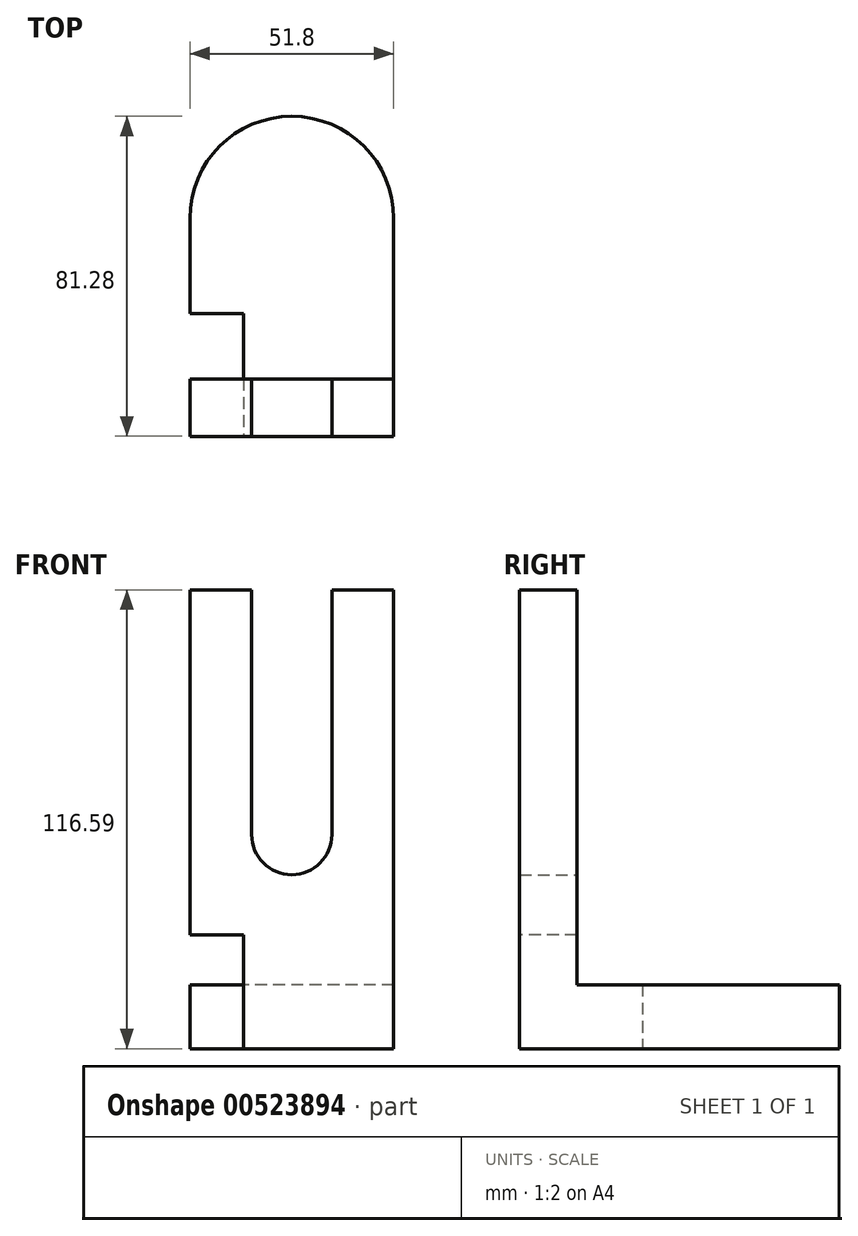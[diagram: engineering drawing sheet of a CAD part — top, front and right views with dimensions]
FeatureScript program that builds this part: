
annotation { "Feature Type Name" : "Feature", "Feature Type Description" : "" }
export const myFeature = defineFeature(function(context is Context, id is Id, definition is map)
    precondition{}
    {
        {
            var Q0;
            Q0=qCreatedBy(makeId("Top.planeOp"),FACE);
            var sketch = newSketch(context, id + "F0", { "sketchPlane" : qUnion([Q0])});
            skLineSegment(sketch, "E0.bottom", {"start": v(25.9, -27.7) * mm, "end": v(-25.9, -27.7) * mm});
            skLineSegment(sketch, "E0.left", {"start": v(25.9, -27.7) * mm, "end": v(25.9, 27.7) * mm});
            skLineSegment(sketch, "E0.right", {"start": v(-25.9, -27.7) * mm, "end": v(-25.9, 27.7) * mm});
            skPoint(sketch, "E0.middle", {"position": v(0, 0) * mm});
            skArc(sketch, "E1", {"start": v(-25.9, 27.7) * mm, "mid": v(0, 53.6) * mm, "end": v(25.9, 27.7) * mm});
            skSolve(sketch);
        }
        {
            var Q0;
            Q0=makeQuery(id+"F0.imprint","IMPRINT",FACE,{"disambiguationData":[TD([[makeQuery(id+"F0.imprint","IMPRINT",EDGE,{"derivedFrom":sQuery(id+"F0.wireOp",EDGE,"E0.bottom")}),-1.0]])]});
            extrude(context, id + "F1", {"entities" : qUnion([Q0]), "depth" : 16.26 * mm, "offsetDistance" : 25.4 * mm});
        }
        {
            var Q0;
            Q0=makeQuery(id+"F1.opExtrude","CAP_FACE",FACE,{"disambiguationData":[OSD([sQuery(id+"F0.wireOp",EDGE,"E0.bottom"),sQuery(id+"F0.wireOp",EDGE,"E0.left"),sQuery(id+"F0.wireOp",EDGE,"E0.right"),sQuery(id+"F0.wireOp",EDGE,"E1")])],"isStart":false});
            var sketch = newSketch(context, id + "F2", { "sketchPlane" : qUnion([Q0])});
            skLineSegment(sketch, "E2.bottom", {"start": v(25.9, -27.7) * mm, "end": v(-25.9, -27.7) * mm});
            skLineSegment(sketch, "E2.top", {"start": v(25.9, -13.13) * mm, "end": v(-25.9, -13.13) * mm});
            skLineSegment(sketch, "E2.left", {"start": v(25.9, -27.7) * mm, "end": v(25.9, -13.13) * mm});
            skLineSegment(sketch, "E2.right", {"start": v(-25.9, -27.7) * mm, "end": v(-25.9, -13.13) * mm});
            skSolve(sketch);
        }
        {
            var Q0;
            Q0=makeQuery(id+"F2.imprint","IMPRINT",FACE,{"disambiguationData":[TD([[makeQuery(id+"F2.imprint","IMPRINT",EDGE,{"derivedFrom":sQuery(id+"F2.wireOp",EDGE,"E2.bottom")}),-1.0]])]});
            extrude(context, id + "F3", {"entities" : qUnion([Q0]), "operationType" : NewBodyOperationType.ADD, "depth" : 100.33 * mm, "offsetDistance" : 25.4 * mm});
        }
        {
            var Q0;
            Q0=makeQuery(id+"F3.opExtrude","SWEPT_FACE",FACE,{"disambiguationData":[OSD([sQuery(id+"F2.wireOp",EDGE,"E2.top")])]});
            var sketch = newSketch(context, id + "F4", { "sketchPlane" : qUnion([Q0])});
            skLineSegment(sketch, "E3.top", {"start": v(10.2, 116.52) * mm, "end": v(-10.2, 116.52) * mm});
            skLineSegment(sketch, "E3.left", {"start": v(10.2, 54.38) * mm, "end": v(10.2, 116.52) * mm});
            skLineSegment(sketch, "E3.right", {"start": v(-10.2, 54.38) * mm, "end": v(-10.2, 116.52) * mm});
            skPoint(sketch, "E3.middle", {"position": v(0, 85.45) * mm});
            skArc(sketch, "E4", {"start": v(10.2, 54.38) * mm, "mid": v(0, 44.18) * mm, "end": v(-10.2, 54.38) * mm});
            skSolve(sketch);
        }
        {
            var Q0;
            Q0=makeQuery(id+"F4.imprint","IMPRINT",FACE,{"disambiguationData":[TD([[makeQuery(id+"F4.imprint","IMPRINT",EDGE,{"derivedFrom":sQuery(id+"F4.wireOp",EDGE,"E3.top")}),1.0]])]});
            extrude(context, id + "F5", {"entities" : qUnion([Q0]), "operationType" : NewBodyOperationType.REMOVE, "oppositeDirection" : true, "depth" : 39.12 * mm, "offsetDistance" : 25.4 * mm});
        }
        {
            var Q0;
            Q0=makeQuery(id+"F5.boolean.opBoolean","COPY",FACE,{"derivedFrom":makeQuery(id+"F5.opExtrude","SWEPT_FACE",FACE,{"disambiguationData":[OSD([sQuery(id+"F4.wireOp",EDGE,"E3.top")])]})});
            extrude(context, id + "F6", {"entities" : qUnion([Q0]), "operationType" : NewBodyOperationType.REMOVE, "oppositeDirection" : true, "depth" : 25.4 * mm, "offsetDistance" : 25.4 * mm});
        }
        {
            var Q0;
            Q0=makeQuery(id+"F3.boolean.opBoolean","MERGE",FACE,{"derivedFrom":[makeQuery(id+"F1.opExtrude","SWEPT_FACE",FACE,{"disambiguationData":[OSD([sQuery(id+"F0.wireOp",EDGE,"E0.bottom")])]}),makeQuery(id+"F3.opExtrude","SWEPT_FACE",FACE,{"disambiguationData":[OSD([sQuery(id+"F2.wireOp",EDGE,"E2.bottom")])]})]});
            var sketch = newSketch(context, id + "F7", { "sketchPlane" : qUnion([Q0])});
            skLineSegment(sketch, "E5.bottom", {"start": v(-25.9, 28.84) * mm, "end": v(-12.22, 28.84) * mm});
            skLineSegment(sketch, "E5.top", {"start": v(-25.9, 0) * mm, "end": v(-12.22, 0) * mm});
            skLineSegment(sketch, "E5.left", {"start": v(-25.9, 28.84) * mm, "end": v(-25.9, 0) * mm});
            skLineSegment(sketch, "E5.right", {"start": v(-12.22, 28.84) * mm, "end": v(-12.22, 0) * mm});
            skSolve(sketch);
        }
        {
            var Q0;
            Q0=makeQuery(id+"F7.imprint","IMPRINT",FACE,{"disambiguationData":[TD([[makeQuery(id+"F7.imprint","IMPRINT",EDGE,{"derivedFrom":sQuery(id+"F7.wireOp",EDGE,"E5.bottom")}),-1.0]])]});
            extrude(context, id + "F8", {"entities" : qUnion([Q0]), "operationType" : NewBodyOperationType.REMOVE, "oppositeDirection" : true, "depth" : 31.24 * mm, "offsetDistance" : 25.4 * mm});
        }
    });
